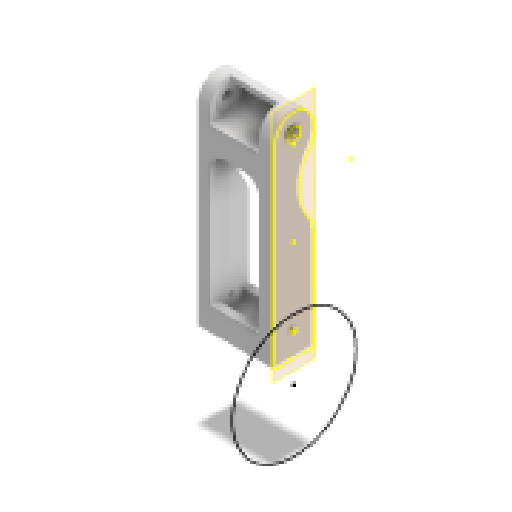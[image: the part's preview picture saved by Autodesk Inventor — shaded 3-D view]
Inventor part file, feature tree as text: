
AUTODESK INVENTOR PART (.ipt)
format: ipt  version: 2025 (Build 290162000, 162)  size: 335,360 bytes
history: native  units: in
note: dims shown in document units (in); Inventor stores cm internally (conversion verified against a paired STEP export)
features: sketch x16, extrude x15, projected_geometry x14, fillet x7, plane x5, other x3, mirror x2, reference x1
ambient origin geometry x8: Origin, YZ Plane, XZ Plane, XY Plane, X Axis, Y Axis, Z Axis, Center Point
bodies: Solid1 (feature_tree)
feature tree (63):
  extrude  "Extrusion1"  Depth=0.315in TaperAngle=0.0deg
  extrude  "Extrusion2"  Depth=0.2559in
  extrude  "Extrusion3"  Depth=0.1181in
  plane  "Work Plane1"
  mirror  "Mirror1"
  extrude  "Extrusion4"  Depth=0.315in TaperAngle=0.0deg
  extrude  "Extrusion5"  Depth=0.5in
  fillet  "Fillet1"  Radius=1.0in
  extrude  "Extrusion6"  Depth=0.4in
  fillet  "Fillet2"  [1 undecoded]
  fillet  "Fillet4"  Radius=0.3228in
  plane  "Work Plane2"
  plane  "Work Plane5"
  sketch  "Sketch16"
  extrude  "Extrusion7"  Depth=1.5in
  fillet  "Fillet5"  Radius=0.2362in
  extrude  "Extrusion8"  Depth=0.3937in
  fillet  "Fillet6"  Radius=0.3937in
  extrude  "Extrusion9"  Depth=0.3937in TaperAngle=0.0deg
  mirror  "Mirror2"
  fillet  "Fillet7"  Radius=1.5507in
  sketch  "Sketch10"  dims[d38=0.4724in d39=0.0in d40=3.0in]
  plane  "Work Plane3"
  extrude  "Extrusion10"  Depth=3.0in
  sketch  "Sketch11"  dims[d41=0.2362in d42=0.0in d43=0.0in d44=0.0in]
  plane  "Work Plane4"
  extrude  "Extrusion11"  TaperAngle=0.0deg  [1 undecoded]
  extrude  "Extrusion12"  Depth=0.0591in TaperAngle=0.0deg
  fillet  "Fillet8"  Radius=0.0787in
  extrude  "Extrusion13"  TaperAngle=0.0deg  [1 undecoded]
  extrude  "Extrusion14"  [1 undecoded]
  extrude  "Extrusion15"  [1 undecoded]
  sketch  "Sketch1"  dims[d0=0.3346in d1=0.315in d2=0.0in]
  sketch  "Sketch2"  dims[d3=0.0787in d4=0.0in d5=0.2559in]
  projected_geometry  "Projected Loop1"
  sketch  "Sketch3"  dims[d6=0.1181in d7=0.0in d8=0.1181in]
  projected_geometry  "Projected Loop2"
  sketch  "Sketch4"  dims[d9=0.6102in d10=0.315in d11=0.0in]
  projected_geometry  "Projected Loop3"
  sketch  "Sketch5"  dims[d12=0.0in d13=0.0in d14=0.5in d15=1.0in d16=0.0in]
  projected_geometry  "Projected Loop4"
  sketch  "Sketch6"  dims[d17=0.25in d19=0.4in d20=-1.0836in d21=0.3228in]
  projected_geometry  "Projected Loop5"
  sketch  "Sketch7"  dims[d22=0.4724in d23=0.0in d24=1.5in d25=0.2362in]
  projected_geometry  "Projected Loop6"
  reference  "Reference1"
  sketch  "Sketch8"  dims[d26=0.1575in d27=0.0in d28=2.0in d29=0.3937in d30=0.0in]
  sketch  "Sketch9"  dims[d31=0.25in d33=-0.2362in d34=0.3937in d35=0.0in d36=1.5507in d37=0.0in]
  projected_geometry  "Projected Loop7"
  projected_geometry  "Projected Loop8"
  projected_geometry  "Projected Loop9"
  sketch  "Sketch12"  dims[d46=0.5087in d51=0.0591in d52=0.0in d53=0.0787in]
  projected_geometry  "Projected Loop10"
  projected_geometry  "Projected Loop11"
  sketch  "Sketch13"  dims[d48=0.0in d49=0.0in]
  sketch  "Sketch14"  dims[d50=0.0in]
  projected_geometry  "Projected Loop12"
  sketch  "Sketch15"
  projected_geometry  "Projected Loop13"
  projected_geometry  "Projected Loop14"
  other  "<userpath>\Desktop\puppycat\singleSwingarmV2.iam"
  other  "singleSwingarmV2.iam"
  other  "6082rsBearing:3"
note: 5 required parameter values undecoded (feature->parameter linkage not recoverable at this tier; creation-order binding heuristic only, values carry confidence <= 0.55)
